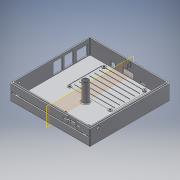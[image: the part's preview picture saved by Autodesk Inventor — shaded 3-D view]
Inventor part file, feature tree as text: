
AUTODESK INVENTOR PART (.ipt)
format: ipt  version: 2018 (Build 220112000, 112)  size: 790,528 bytes
history: native  units: in
note: dims shown in document units (in); Inventor stores cm internally (conversion verified against a paired STEP export)
features: extrude x34, sketch x30, projected_geometry x8, reference x7, plane x6, fillet x5, thread x4, other x3, mirror x1
ambient origin geometry x8: Origin, YZ Plane, XZ Plane, XY Plane, X Axis, Y Axis, Z Axis, Center Point
bodies: Solid1 (feature_tree)
feature tree (98):
  extrude  "Extrusion1"  Depth=4.5in
  extrude  "Extrusion4"  Depth=0.1in
  sketch  "Sketch6"  dims[d12=0.7874in d13=0.0in d17=2.2047in]
  extrude  "Extrusion5"  Depth=0.7874in
  extrude  "Extrusion6"  Depth=0.4035in
  extrude  "Extrusion7"  Depth=0.6299in
  extrude  "Extrusion8"  Depth=0.2589in
  extrude  "Extrusion9"  Depth=0.2589in
  extrude  "Extrusion10"  Depth=0.314in
  extrude  "Extrusion11"  Depth=0.1575in
  extrude  "Extrusion12"  Depth=0.1575in
  thread  "Thread1"  [1 undecoded]
  thread  "Thread2"  [1 undecoded]
  thread  "Thread3"  [1 undecoded]
  thread  "Thread4"  [1 undecoded]
  extrude  "Extrusion13"  Depth=0.689in TaperAngle=0.0deg
  extrude  "Extrusion14"  Depth=0.2953in TaperAngle=0.0deg
  extrude  "Extrusion15"  Depth=0.1378in TaperAngle=0.0deg
  fillet  "Fillet1"  Radius=0.0394in
  extrude  "Extrusion16"  Depth=0.1378in
  extrude  "Extrusion17"  Depth=0.1378in
  fillet  "Fillet3"  Radius=0.1378in
  extrude  "Extrusion18"  Depth=2.2835in
  extrude  "Extrusion19"  Depth=2.2835in
  plane  "Work Plane1"
  extrude  "Extrusion20"  Depth=0.05in
  extrude  "Extrusion21"  Depth=0.05in
  fillet  "Fillet4"  Radius=0.05in
  plane  "Work Plane2"
  extrude  "Extrusion22"  Depth=0.075in TaperAngle=0.0deg
  extrude  "Extrusion23"  Depth=1.0in TaperAngle=0.0deg
  extrude  "Extrusion24"  Depth=1.0in TaperAngle=0.0deg
  extrude  "Extrusion25"  Depth=0.075in
  extrude  "Extrusion26"  Depth=0.075in
  extrude  "Extrusion27"  Depth=0.05in TaperAngle=0.0deg
  extrude  "Extrusion28"  Depth=0.05in TaperAngle=0.0deg
  extrude  "Extrusion29"  Depth=0.45in
  plane  "Work Plane3"
  mirror  "Mirror1"
  sketch  "Sketch27"  dims[d82=0.05in d83=0.0in d84=0.075in]
  plane  "Work Plane4"
  extrude  "Extrusion30"  Depth=0.05in
  extrude  "Extrusion31"  Depth=0.05in TaperAngle=0.0deg
  extrude  "Extrusion32"  Depth=0.175in
  fillet  "Fillet5"  Radius=0.05in
  extrude  "Extrusion33"  Depth=0.05in
  extrude  "Extrusion34"  Depth=0.01in
  sketch  "Sketch32"  dims[d97=0.05in d98=0.05in d99=0.0in]
  plane  "Work Plane5"
  extrude  "Extrusion35"  Depth=0.2in
  fillet  "Fillet6"  [1 undecoded]
  sketch  "Sketch33"  dims[d100=0.175in d101=0.175in d102=0.05in d103=0.0in d104=0.05in d105=0.0875in d106=0.2in d107=90.0deg d108=0.9449in d109=0.0275in d110=0.0275in d111=0.0275in d112=0.9174in d115=0.05in d116=0.0in d117=0.25in d118=0.25in d119=0.05in d120=0.05in d121=0.0in d122=0.05in d123=0.025in d124=0.025in d125=0.025in d126=0.025in d127=0.075in d128=0.3in d129=0.0in d130=0.3in d131=0.0in d132=0.05in d133=0.225in d134=0.1in d135=0.1in d136=0.1in d137=0.025in d138=0.05in d139=0.1in d140=0.1in d141=0.1in d142=0.025in d143=0.05in d144=0.3in d145=0.0in d146=0.05in d147=0.0in d148=0.05in d149=0.0in d150=0.05in d151=0.05in d152=0.05in d153=0.0in d154=0.25in d155=0.25in d156=0.025in d157=0.025in d158=0.25in d159=0.025in d160=0.25in d161=0.025in d162=0.25in d163=0.025in d164=0.25in d165=0.025in d166=0.0125in d167=0.0125in d168=0.05in d169=0.0in d172=0.125in d173=0.125in d174=0.025in d175=0.025in d176=0.0in d177=0.04in d178=0.05in d179=0.0in d180=0.05in d181=0.0in d182=0.0059in d183=0.05in d184=0.01in d185=0.05in d186=0.0in d187=0.01in d188=0.0in d189=0.05in d190=0.0in d191=0.02in d192=0.025in d193=0.025in d194=0.025in d195=0.025in d196=0.025in d197=0.0in d198=0.25in d199=0.25in d200=0.25in d201=0.25in d202=0.25in d203=0.01in d204=0.01in d205=0.01in d206=0.01in d207=0.01in d208=0.0in d209=0.25in d210=0.3in d211=0.025in d212=0.01in d213=0.0in d214=0.05in d215=0.0125in d217=0.0125in d218=0.0125in d219=0.01in d220=0.0in]
  plane  "Work Plane6"
  extrude  "Extrusion36"  Depth=0.01in
  sketch  "Sketch1"  dims[d0=4.5in d1=4.5in]
  sketch  "Sketch4"  dims[d2=0.1in d3=0.0in d11=0.1in]
  projected_geometry  "Projected Loop3"
  sketch  "Sketch7"  dims[d18=3.3465in d21=0.4035in]
  sketch  "Sketch8"  dims[d22=0.7382in d23=0.6299in]
  sketch  "Sketch9"  dims[d24=0.2589in d25=0.2589in]
  projected_geometry  "Projected Loop4"
  projected_geometry  "Projected Loop5"
  projected_geometry  "Projected Loop6"
  sketch  "Sketch10"  dims[d26=0.2589in d27=0.2589in]
  sketch  "Sketch11"  dims[d28=0.314in d29=0.314in]
  sketch  "Sketch12"  dims[d30=0.4173in d31=0.1575in]
  sketch  "Sketch13"  dims[d32=0.1575in d33=0.8425in d34=0.3051in d35=0.3051in d37=0.8465in d38=0.128in]
  sketch  "Sketch14"  dims[d39=0.128in d40=0.689in d41=0.0in]
  sketch  "Sketch15"  dims[d42=0.5906in d43=0.0in d44=0.2953in d45=0.0in]
  sketch  "Sketch16"  dims[d46=0.315in d47=0.0in d48=0.1378in d49=0.0in d50=0.0394in d51=0.0in]
  sketch  "Sketch17"  dims[d52=0.1378in d53=0.1378in]
  sketch  "Sketch18"  dims[d54=0.0925in d56=0.1378in d57=0.1378in]
  projected_geometry  "Projected Loop7"
  sketch  "Sketch19"  dims[d58=0.0925in d59=2.2835in]
  sketch  "Sketch20"  dims[d60=0.0925in d61=2.2835in]
  sketch  "Sketch21"  dims[d62=0.0925in d63=0.05in]
  sketch  "Sketch22"  dims[d64=0.05in d65=0.05in d66=0.05in]
  sketch  "Sketch23"  dims[d67=0.0197in d68=0.0in d69=0.075in d70=0.0in]
  sketch  "Sketch24"  dims[d71=1.0in d72=0.0in d73=1.0in d74=0.0in]
  projected_geometry  "Projected Loop8"
  projected_geometry  "Projected Loop9"
  sketch  "Sketch25"  dims[d75=1.0in d76=0.0in d77=1.0in d78=0.0in]
  reference  "Reference1"
  sketch  "Sketch26"  dims[d79=0.075in d81=0.064in]
  reference  "Reference2"
  reference  "Reference3"
  reference  "Reference4"
  reference  "Reference5"
  sketch  "Sketch28"  dims[d86=0.064in d87=0.05in d88=0.0in]
  projected_geometry  "Projected Loop10"
  sketch  "Sketch29"  dims[d89=0.05in d90=0.05in d91=0.0in]
  sketch  "Sketch30"  dims[d92=0.05in d94=0.45in]
  sketch  "Sketch31"  dims[d95=0.075in d96=0.05in]
  reference  "Reference6"
  reference  "Reference7"
  other  "<userpath>\Documents\Commodore Cube Project\Case\Assembly.iam"
  other  "Assembly.iam"
  other  "Dome:1"
note: 5 required parameter values undecoded (feature->parameter linkage not recoverable at this tier; creation-order binding heuristic only, values carry confidence <= 0.55)
